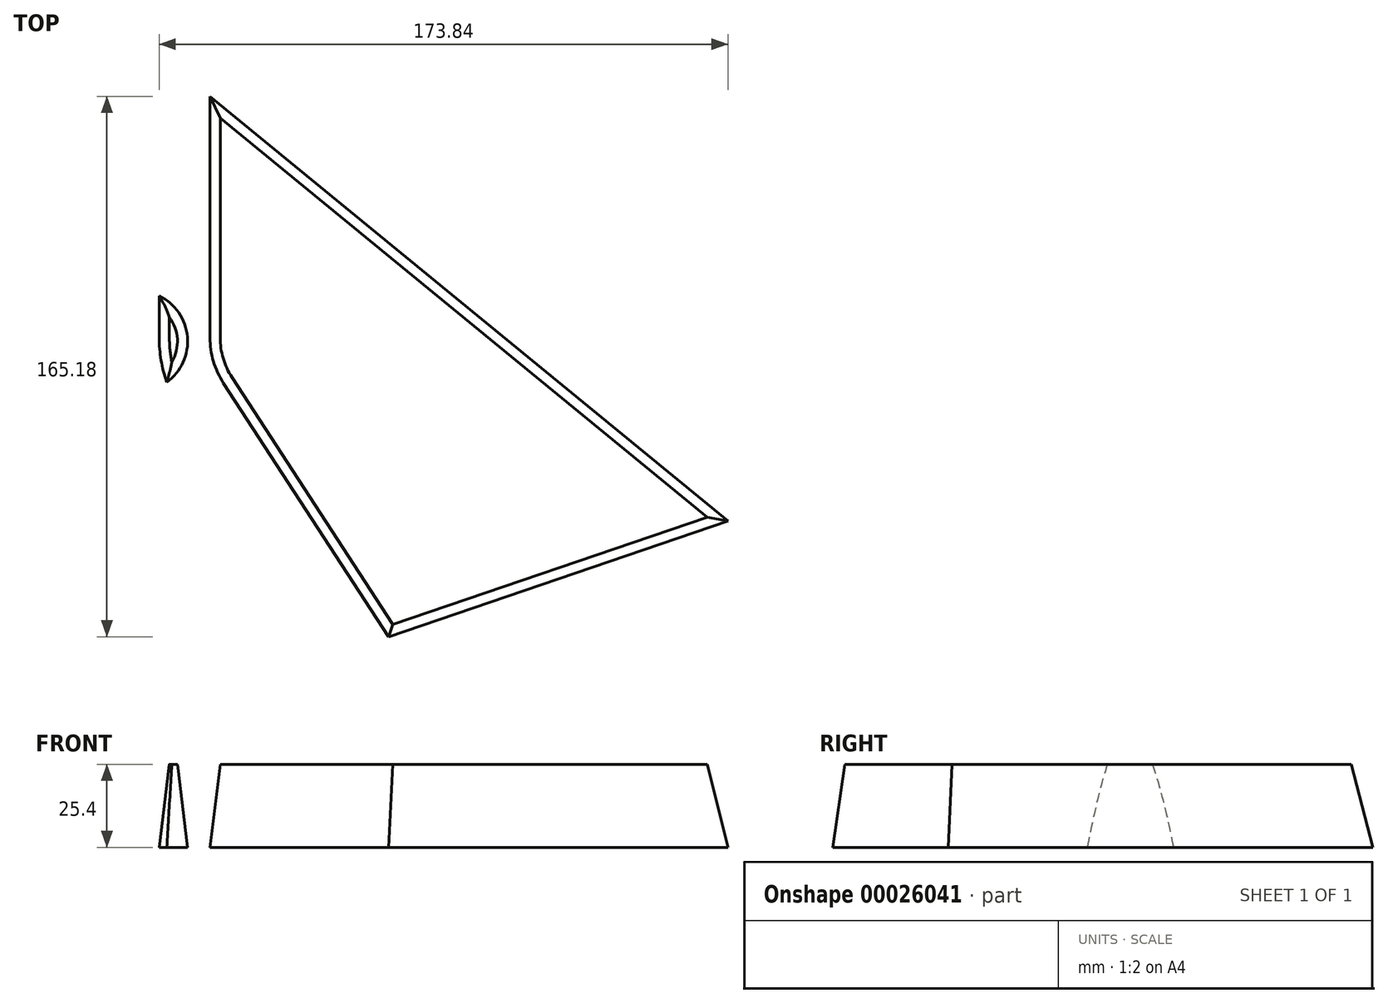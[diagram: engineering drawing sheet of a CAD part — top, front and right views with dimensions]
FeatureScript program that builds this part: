
annotation { "Feature Type Name" : "Feature", "Feature Type Description" : "" }
export const myFeature = defineFeature(function(context is Context, id is Id, definition is map)
    precondition{}
    {
        {
            var Q0;
            Q0=qCreatedBy(makeId("Top.planeOp"),FACE);
            var sketch = newSketch(context, id + "F0", { "sketchPlane" : qUnion([Q0])});
            skLineSegment(sketch, "E0", {"start": v(-93.8, 18.24) * mm, "end": v(-43.34, -59.34) * mm});
            skLineSegment(sketch, "E1", {"start": v(-43.34, -59.34) * mm, "end": v(60.4, -23.95) * mm});
            skLineSegment(sketch, "E2", {"start": v(60.4, -23.95) * mm, "end": v(-97.9, 105.84) * mm});
            skLineSegment(sketch, "E3", {"start": v(-97.9, 105.84) * mm, "end": v(-97.9, 32.09) * mm});
            skArc(sketch, "E4", {"start": v(-111.58, 18.15) * mm, "mid": v(-108.69, 41.28) * mm, "end": v(-132, 40.86) * mm});
            skPoint(sketch, "E5.visualSharp", {"position": v(-97.9, 24.55) * mm});
            skArc(sketch, "E5.filletArc", {"start": v(-97.9, 32.09) * mm, "mid": v(-96.85, 24.86) * mm, "end": v(-93.8, 18.24) * mm});
            skLineSegment(sketch, "E6.0", {"start": v(-106.81, 9.77) * mm, "end": v(-56.36, -67.8) * mm});
            skArc(sketch, "E6.1", {"start": v(-113.43, 32.09) * mm, "mid": v(-111.74, 20.45) * mm, "end": v(-106.81, 9.77) * mm});
            skLineSegment(sketch, "E6.2", {"start": v(-113.43, 138.65) * mm, "end": v(-113.43, 32.09) * mm});
            skLineSegment(sketch, "E6.3", {"start": v(70.25, -11.95) * mm, "end": v(-113.43, 138.65) * mm});
            skSolve(sketch);
        }
        {
            var Q0;
            Q0=makeQuery(id+"F0.imprint","IMPRINT",FACE,{"disambiguationData":[TD([[makeQuery(id+"F0.imprint","IMPRINT",EDGE,{"derivedFrom":sQuery(id+"F0.wireOp",EDGE,"E0")}),1.0]])]});
            var Q1;
            {var subQ1=sQuery(id+"F0.wireOp",EDGE,"E4");var subQ3=sQuery(id+"F0.wireOp",EDGE,"E6.1");var subQ5=makeQuery(id+"F0.imprint","INTERSECT",VERTEX,{"derivedFrom":[subQ1,subQ3]});Q1=makeQuery(id+"F0.imprint","IMPRINT",FACE,{"disambiguationData":[TD([[makeQuery(id+"F0.imprint","IMPRINT",EDGE,{"disambiguationData":[TD([[subQ5,-1.0]])],"derivedFrom":subQ1}),1.0]])]});}
            extrude(context, id + "F1", {"entities" : qUnion([Q0, Q1]), "depth" : 25.4 * mm, "hasDraft" : true, "draftAngle" : 7 * degree, "draftPullDirection" : true});
        }
    });
